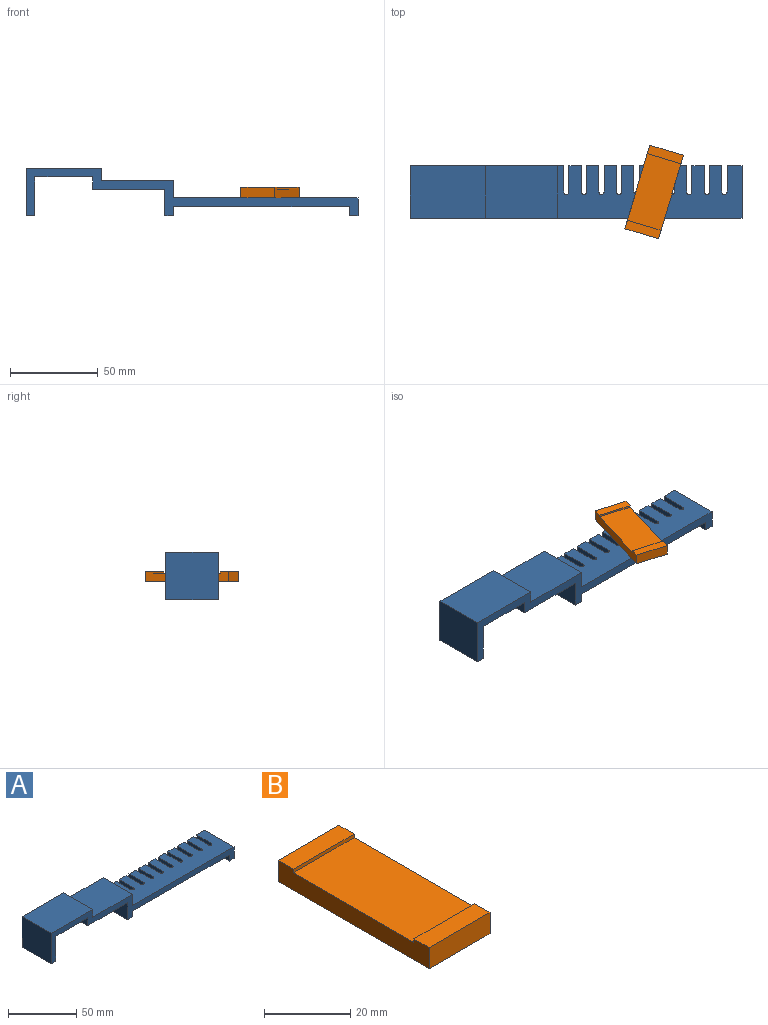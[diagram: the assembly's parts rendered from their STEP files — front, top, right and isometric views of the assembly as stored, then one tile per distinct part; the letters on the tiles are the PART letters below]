
ASSEMBLY  parts=2 mates=1
PART A: 60 faces, bbox 189x30x27.2 mm
  f0: plane 100x30mm, normal (0,0,-1), area 2514.7mm2, adj f1,f2,f3,f4,f5,f6,f7,f8
  f1: plane 10.2x8.5mm, normal (0,1,0), area 68.5mm2, adj f0,f19,f20,f21,f22,f57
  f2: plane 7x5mm, normal (0,1,0), area 35mm2, adj f0,f22,f56,f59
  f3: plane 7x5mm, normal (0,1,0), area 35mm2, adj f0,f22,f53,f55
  f4: plane 7x5mm, normal (0,1,0), area 35mm2, adj f0,f22,f50,f52
  f5: plane 7x5mm, normal (0,1,0), area 35mm2, adj f0,f22,f47,f49
  f6: plane 7x5mm, normal (0,1,0), area 35mm2, adj f0,f22,f44,f46
  f7: plane 7x5mm, normal (0,1,0), area 35mm2, adj f0,f22,f41,f43
  f8: plane 7x5mm, normal (0,1,0), area 35mm2, adj f0,f22,f38,f40
  f9: plane 7x5mm, normal (0,1,0), area 35mm2, adj f0,f22,f35,f37
  f10: plane 7x5mm, normal (0,1,0), area 35mm2, adj f0,f22,f32,f34
  f11: plane 30x5mm, normal (0,0,-1), area 150mm2, adj f12,f27,f28,f29
  f12: plane 30x22.2mm, normal (1,0,0), area 666mm2, adj f11,f13,f28,f29
  f13: plane 33x30mm, normal (0,0,-1), area 990mm2, adj f12,f14,f28,f29
  f14: plane 30x7mm, normal (-1,0,0), area 210mm2, adj f13,f15,f28,f29
  f15: plane 41x30mm, normal (0,0,-1), area 1230mm2, adj f14,f16,f28,f29
  f16: plane 30x15.2mm, normal (-1,0,0), area 456mm2, adj f15,f17,f28,f29
  f17: plane 30x5mm, normal (0,0,-1), area 150mm2, adj f16,f18,f28,f29
  f18: plane 30x5.2mm, normal (1,0,0), area 156mm2, adj f0,f17,f28,f29
  f19: plane 30x5.2mm, normal (-1,0,0), area 156mm2, adj f0,f1,f20,f28
  f20: plane 30x5mm, normal (0,0,-1), area 150mm2, adj f1,f19,f21,f28
  f21: plane 30x10.2mm, normal (1,0,0), area 306mm2, adj f1,f20,f22,f28
  f22: plane 105x30mm, normal (0,0,1), area 2664.7mm2, adj f1,f2,f3,f4,f5,f6,f7,f8
  f23: plane 30x10mm, normal (1,0,0), area 300mm2, adj f22,f24,f28,f29
  f24: plane 41x30mm, normal (0,0,1), area 1230mm2, adj f23,f25,f28,f29
  f25: plane 30x7mm, normal (1,0,0), area 210mm2, adj f24,f26,f28,f29
  f26: plane 43x30mm, normal (0,0,1), area 1290mm2, adj f25,f27,f28,f29
  f27: plane 30x27.2mm, normal (-1,0,0), area 816mm2, adj f11,f26,f28,f29
  f28: plane 189x27.2mm, normal (0,-1,0), area 1193mm2, adj f0,f11,f12,f13,f14,f15,f16,f17
  f29: plane 87.5x27.2mm, normal (0,1,0), area 659.5mm2, adj f0,f11,f12,f13,f14,f15,f16,f17
  f30: cylinder r=1.5mm len=5mm, axis (0,0,-1), area 23.6mm2, adj f0,f22,f31,f32
  f31: plane 15x5mm, normal (1,0,0), area 75mm2, adj f0,f22,f29,f30
  f32: plane 15x5mm, normal (-1,0,0), area 75mm2, adj f0,f10,f22,f30
  f33: cylinder r=1.5mm len=5mm, axis (0,0,-1), area 23.6mm2, adj f0,f22,f34,f35
  f34: plane 15x5mm, normal (1,0,0), area 75mm2, adj f0,f10,f22,f33
  f35: plane 15x5mm, normal (-1,0,0), area 75mm2, adj f0,f9,f22,f33
  f36: cylinder r=1.5mm len=5mm, axis (0,0,-1), area 23.6mm2, adj f0,f22,f37,f38
  f37: plane 15x5mm, normal (1,0,0), area 75mm2, adj f0,f9,f22,f36
  f38: plane 15x5mm, normal (-1,0,0), area 75mm2, adj f0,f8,f22,f36
  f39: cylinder r=1.5mm len=5mm, axis (0,0,-1), area 23.6mm2, adj f0,f22,f40,f41
  f40: plane 15x5mm, normal (1,0,0), area 75mm2, adj f0,f8,f22,f39
  f41: plane 15x5mm, normal (-1,0,0), area 75mm2, adj f0,f7,f22,f39
  f42: cylinder r=1.5mm len=5mm, axis (0,0,-1), area 23.6mm2, adj f0,f22,f43,f44
  f43: plane 15x5mm, normal (1,0,0), area 75mm2, adj f0,f7,f22,f42
  f44: plane 15x5mm, normal (-1,0,0), area 75mm2, adj f0,f6,f22,f42
  f45: cylinder r=1.5mm len=5mm, axis (0,0,-1), area 23.6mm2, adj f0,f22,f46,f47
  f46: plane 15x5mm, normal (1,0,0), area 75mm2, adj f0,f6,f22,f45
  f47: plane 15x5mm, normal (-1,0,0), area 75mm2, adj f0,f5,f22,f45
  f48: cylinder r=1.5mm len=5mm, axis (0,0,-1), area 23.6mm2, adj f0,f22,f49,f50
  f49: plane 15x5mm, normal (1,0,0), area 75mm2, adj f0,f5,f22,f48
  f50: plane 15x5mm, normal (-1,0,0), area 75mm2, adj f0,f4,f22,f48
  f51: cylinder r=1.5mm len=5mm, axis (0,0,-1), area 23.6mm2, adj f0,f22,f52,f53
  f52: plane 15x5mm, normal (1,0,0), area 75mm2, adj f0,f4,f22,f51
  f53: plane 15x5mm, normal (-1,0,0), area 75mm2, adj f0,f3,f22,f51
  f54: cylinder r=1.5mm len=5mm, axis (0,0,-1), area 23.6mm2, adj f0,f22,f55,f56
  f55: plane 15x5mm, normal (1,0,0), area 75mm2, adj f0,f3,f22,f54
  f56: plane 15x5mm, normal (-1,0,0), area 75mm2, adj f0,f2,f22,f54
  f57: plane 15x5mm, normal (-1,0,0), area 75mm2, adj f0,f1,f22,f58
  f58: cylinder r=1.5mm len=5mm, axis (0,0,-1), area 23.6mm2, adj f0,f22,f57,f59
  f59: plane 15x5mm, normal (1,0,0), area 75mm2, adj f0,f2,f22,f58
PART B: 12 faces, bbox 20x49.6x11 mm
  f0: cylinder r=1.5mm len=5mm, axis (0,0,1), area 47.1mm2, adj f1,f5
  f1: plane 3x3mm, normal (0,0,-1), area 7.1mm2, adj f0
  f2: plane 49.6x6mm, normal (-1,0,0), area 258mm2, adj f4,f5,f6,f7,f8,f9,f10,f11
  f3: plane 49.6x6mm, normal (1,0,0), area 258mm2, adj f4,f5,f6,f7,f8,f9,f10,f11
  f4: plane 39.6x20mm, normal (0,0,1), area 792mm2, adj f2,f3,f6,f9
  f5: plane 49.6x20mm, normal (0,0,-1), area 984.9mm2, adj f0,f2,f3,f7,f10
  f6: plane 20x1mm, normal (0,-1,0), area 20mm2, adj f2,f3,f4,f8
  f7: plane 20x6mm, normal (0,1,0), area 120mm2, adj f2,f3,f5,f8
  f8: plane 20x5mm, normal (0,0,1), area 100mm2, adj f2,f3,f6,f7
  f9: plane 20x1mm, normal (0,1,0), area 20mm2, adj f2,f3,f4,f11
  f10: plane 20x6mm, normal (0,-1,0), area 120mm2, adj f2,f3,f5,f11
  f11: plane 20x5mm, normal (0,0,1), area 100mm2, adj f2,f3,f9,f10
PLACE A t=(-43.29,0,0.13)mm fixed
PLACE B rot(axis=(0,0,-1),16.6deg) t=(57.71,0,10.33)mm
MATE cylindrical B.f0 <-> A.f45  axis (0,0,-1) through (57.71,0,5.33)mm
